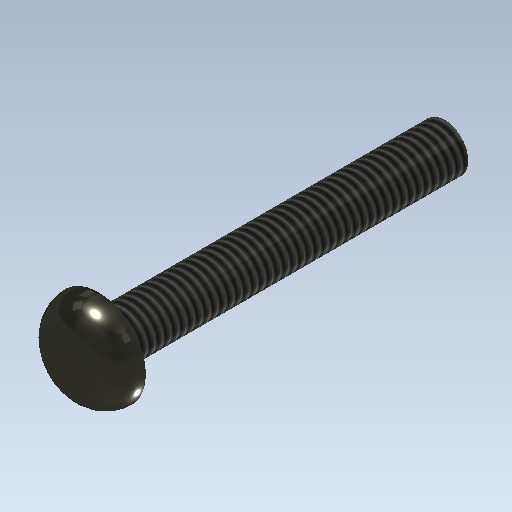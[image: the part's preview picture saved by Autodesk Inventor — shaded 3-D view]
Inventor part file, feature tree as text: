
AUTODESK INVENTOR PART (.ipt)
format: ipt  version: 2020.2 (Build 242310000, 310)  size: 165,888 bytes
history: native  units: mm
features: extrude x4, sketch x4, other x1, fillet x1, thread x1
ambient origin geometry x1: Origin
bodies: Body1 (feature_tree)
feature tree (11):
  other  "ソリッド1"
  extrude  "押し出し1"  Depth=3.0mm
  extrude  "押し出し2"  Depth=6.0mm TaperAngle=0.0deg
  fillet  "フィレット1"  Radius=6.0mm
  thread  "ねじ1"
  extrude  "押し出し3"  Depth=2.0mm TaperAngle=0.0deg
  extrude  "押し出し4"  Depth=2.0mm
  sketch  "スケッチ1"
  sketch  "スケッチ2"
  sketch  "スケッチ3"
  sketch  "スケッチ4"
